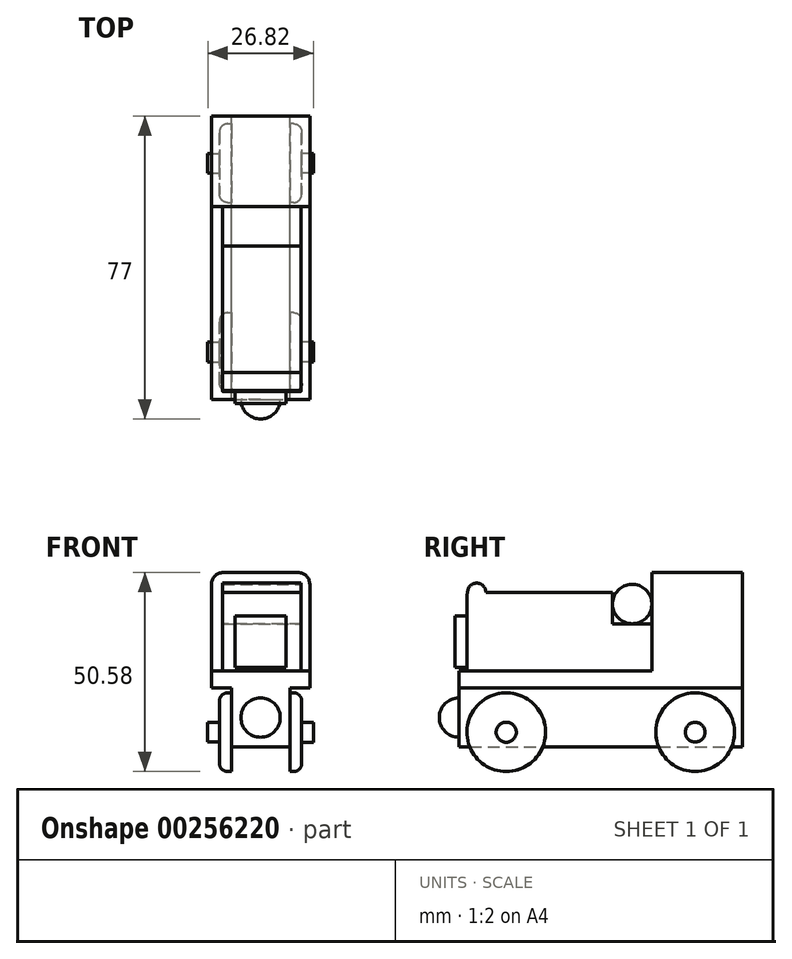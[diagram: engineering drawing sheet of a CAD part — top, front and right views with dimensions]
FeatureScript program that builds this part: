
annotation { "Feature Type Name" : "Feature", "Feature Type Description" : "" }
export const myFeature = defineFeature(function(context is Context, id is Id, definition is map)
    precondition{}
    {
        {
            var Q0;
            Q0=qCreatedBy(makeId("Front.planeOp"),FACE);
            var sketch = newSketch(context, id + "F0", { "sketchPlane" : qUnion([Q0])});
            skLineSegment(sketch, "E0.bottom", {"start": v(-9.68, 12.6) * mm, "end": v(10.32, 12.6) * mm});
            skLineSegment(sketch, "E0.top", {"start": v(-9.68, -7.4) * mm, "end": v(10.32, -7.4) * mm});
            skLineSegment(sketch, "E0.left", {"start": v(-9.68, 12.6) * mm, "end": v(-9.68, -7.4) * mm});
            skLineSegment(sketch, "E0.right", {"start": v(10.32, 12.6) * mm, "end": v(10.32, -7.4) * mm});
            skSolve(sketch);
        }
        {
            var Q0;
            Q0 = qSketchRegion(id + "F0", true);
            extrude(context, id + "F1", {"entities" : qUnion([Q0]), "endBound" : BoundingType.SYMMETRIC, "depth" : 10 * mm});
        }
        {
            var Q0;
            Q0=makeQuery(id+"F1.opExtrude","CAP_FACE",FACE,{"disambiguationData":[OSD([sQuery(id+"F0.wireOp",EDGE,"E0.bottom"),sQuery(id+"F0.wireOp",EDGE,"E0.top"),sQuery(id+"F0.wireOp",EDGE,"E0.left"),sQuery(id+"F0.wireOp",EDGE,"E0.right")])],"isStart":true});
            var sketch = newSketch(context, id + "F2", { "sketchPlane" : qUnion([Q0])});
            skLineSegment(sketch, "E1.bottom", {"start": v(-10.32, 12.6) * mm, "end": v(9.68, 12.6) * mm});
            skLineSegment(sketch, "E1.top", {"start": v(-10.32, 4.6) * mm, "end": v(9.68, 4.6) * mm});
            skLineSegment(sketch, "E1.left", {"start": v(-10.32, 12.6) * mm, "end": v(-10.32, 4.6) * mm});
            skLineSegment(sketch, "E1.right", {"start": v(9.68, 12.6) * mm, "end": v(9.68, 4.6) * mm});
            skSolve(sketch);
        }
        {
            var Q0;
            Q0 = qSketchRegion(id + "F2", true);
            extrude(context, id + "F3", {"entities" : qUnion([Q0]), "operationType" : NewBodyOperationType.ADD, "depth" : 27 * mm});
        }
        {
            var Q0;
            Q0=makeQuery(id+"F1.opExtrude","CAP_FACE",FACE,{"disambiguationData":[OSD([sQuery(id+"F0.wireOp",EDGE,"E0.bottom"),sQuery(id+"F0.wireOp",EDGE,"E0.top"),sQuery(id+"F0.wireOp",EDGE,"E0.left"),sQuery(id+"F0.wireOp",EDGE,"E0.right")])],"isStart":true});
            var sketch = newSketch(context, id + "F4", { "sketchPlane" : qUnion([Q0])});
            skLineSegment(sketch, "E2.bottom", {"start": v(-10.32, 4.6) * mm, "end": v(9.68, 4.6) * mm});
            skLineSegment(sketch, "E2.top", {"start": v(-10.32, -7.4) * mm, "end": v(9.68, -7.4) * mm});
            skLineSegment(sketch, "E2.left", {"start": v(-10.32, 4.6) * mm, "end": v(-10.32, -7.4) * mm});
            skLineSegment(sketch, "E2.right", {"start": v(9.68, 4.6) * mm, "end": v(9.68, -7.4) * mm});
            skSolve(sketch);
        }
        {
            var Q0;
            Q0 = qSketchRegion(id + "F4", true);
            extrude(context, id + "F5", {"entities" : qUnion([Q0]), "operationType" : NewBodyOperationType.ADD, "depth" : 37 * mm});
        }
        {
            var Q0;
            Q0=qCreatedBy(makeId("Front.planeOp"),FACE);
            var sketch = newSketch(context, id + "F6", { "sketchPlane" : qUnion([Q0])});
            skLineSegment(sketch, "E3.bottom", {"start": v(-12.5, -7.4) * mm, "end": v(12.5, -7.4) * mm});
            skLineSegment(sketch, "E3.top", {"start": v(-12.5, -11.76) * mm, "end": v(12.5, -11.76) * mm});
            skLineSegment(sketch, "E3.left", {"start": v(-12.5, -7.4) * mm, "end": v(-12.5, -11.76) * mm});
            skLineSegment(sketch, "E3.right", {"start": v(12.5, -7.4) * mm, "end": v(12.5, -11.76) * mm});
            skPoint(sketch, "E3.middle", {"position": v(0, -9.58) * mm});
            skSolve(sketch);
        }
        {
            var Q0;
            Q0=makeQuery(id+"F6.imprint","IMPRINT",FACE,{"disambiguationData":[TD([[makeQuery(id+"F6.imprint","IMPRINT",EDGE,{"derivedFrom":sQuery(id+"F6.wireOp",EDGE,"E3.bottom")}),-1.0]])]});
            extrude(context, id + "F7", {"entities" : qUnion([Q0]), "operationType" : NewBodyOperationType.ADD, "oppositeDirection" : true, "depth" : 65 * mm});
        }
        {
            var Q0;
            Q0=makeQuery(id+"F7.opExtrude","CAP_FACE",FACE,{"disambiguationData":[OSD([sQuery(id+"F6.wireOp",EDGE,"E3.bottom"),sQuery(id+"F6.wireOp",EDGE,"E3.top"),sQuery(id+"F6.wireOp",EDGE,"E3.left"),sQuery(id+"F6.wireOp",EDGE,"E3.right")])],"isStart":true});
            var sketch = newSketch(context, id + "F8", { "sketchPlane" : qUnion([Q0])});
            skLineSegment(sketch, "E4.bottom", {"start": v(-12.5, -7.4) * mm, "end": v(12.5, -7.4) * mm});
            skLineSegment(sketch, "E4.top", {"start": v(-12.5, -11.76) * mm, "end": v(12.5, -11.76) * mm});
            skLineSegment(sketch, "E4.left", {"start": v(-12.5, -7.4) * mm, "end": v(-12.5, -11.76) * mm});
            skLineSegment(sketch, "E4.right", {"start": v(12.5, -7.4) * mm, "end": v(12.5, -11.76) * mm});
            skSolve(sketch);
        }
        {
            var Q0;
            Q0 = qSketchRegion(id + "F8", true);
            extrude(context, id + "F9", {"entities" : qUnion([Q0]), "operationType" : NewBodyOperationType.ADD, "depth" : 7 * mm});
        }
        {
            var Q0;
            Q0=makeQuery(id+"F9.boolean.opBoolean","MERGE",FACE,{"derivedFrom":[makeQuery(id+"F7.opExtrude","SWEPT_FACE",FACE,{"disambiguationData":[OSD([sQuery(id+"F6.wireOp",EDGE,"E3.bottom")])]}),makeQuery(id+"F9.opExtrude","SWEPT_FACE",FACE,{"disambiguationData":[OSD([sQuery(id+"F8.wireOp",EDGE,"E4.bottom")])]})]});
            var sketch = newSketch(context, id + "F10", { "sketchPlane" : qUnion([Q0])});
            skLineSegment(sketch, "E5.bottom", {"start": v(-12.5, 42) * mm, "end": v(12.5, 42) * mm});
            skLineSegment(sketch, "E5.top", {"start": v(-12.5, 65) * mm, "end": v(12.5, 65) * mm});
            skLineSegment(sketch, "E5.left", {"start": v(-12.5, 42) * mm, "end": v(-12.5, 65) * mm});
            skLineSegment(sketch, "E5.right", {"start": v(12.5, 42) * mm, "end": v(12.5, 65) * mm});
            skSolve(sketch);
        }
        {
            var Q0;
            Q0 = qSketchRegion(id + "F10", true);
            extrude(context, id + "F11", {"entities" : qUnion([Q0]), "operationType" : NewBodyOperationType.ADD, "depth" : 25 * mm});
        }
        {
            var Q0;
            Q0=makeQuery(id+"F5.boolean.opBoolean","MERGE",FACE,{"derivedFrom":[makeQuery(id+"F3.boolean.opBoolean","MERGE",FACE,{"derivedFrom":[makeQuery(id+"F1.opExtrude","SWEPT_FACE",FACE,{"disambiguationData":[OSD([sQuery(id+"F0.wireOp",EDGE,"E0.right")])]}),makeQuery(id+"F3.opExtrude","SWEPT_FACE",FACE,{"disambiguationData":[OSD([sQuery(id+"F2.wireOp",EDGE,"E1.left")])]})]}),makeQuery(id+"F5.opExtrude","SWEPT_FACE",FACE,{"disambiguationData":[OSD([sQuery(id+"F4.wireOp",EDGE,"E2.left")])]})]});
            var sketch = newSketch(context, id + "F12", { "sketchPlane" : qUnion([Q0])});
            skLineSegment(sketch, "E6", {"start": v(42, 4.6) * mm, "end": v(42, 17.55) * mm, "construction": true});
            skPoint(sketch, "E7.first.point", {"position": v(37, 4.6) * mm});
            skPoint(sketch, "E7.second.point", {"position": v(32, 8.6) * mm});
            skPoint(sketch, "E7.third.point", {"position": v(42, 9.37) * mm});
            skCircle(sketch, "E8", {"center": v(37, 9.6) * mm, "radius": 5 * mm});
            skPoint(sketch, "E8.third.point", {"position": v(32, 9.37) * mm});
            skSolve(sketch);
        }
        {
            var Q0;
            Q0 = qSketchRegion(id + "F12", true);
            extrude(context, id + "F13", {"entities" : qUnion([Q0]), "oppositeDirection" : true, "depth" : 20 * mm});
        }
        {
            var Q0;
            Q0=makeQuery(id+"F9.boolean.opBoolean","MERGE",FACE,{"derivedFrom":[makeQuery(id+"F7.opExtrude","SWEPT_FACE",FACE,{"disambiguationData":[OSD([sQuery(id+"F6.wireOp",EDGE,"E3.top")])]}),makeQuery(id+"F9.opExtrude","SWEPT_FACE",FACE,{"disambiguationData":[OSD([sQuery(id+"F8.wireOp",EDGE,"E4.top")])]})]});
            var sketch = newSketch(context, id + "F14", { "sketchPlane" : qUnion([Q0])});
            skLineSegment(sketch, "E9", {"start": v(-12.5, -29) * mm, "end": v(-7.5, -29) * mm, "construction": true});
            skLineSegment(sketch, "E10", {"start": v(12.5, -29) * mm, "end": v(7.5, -29) * mm, "construction": true});
            skPoint(sketch, "E10.endSnap0", {"position": v(12.5, -29) * mm});
            skLineSegment(sketch, "E11.bottom", {"start": v(7.41, 7) * mm, "end": v(-7.41, 7) * mm});
            skLineSegment(sketch, "E11.top", {"start": v(7.41, -65) * mm, "end": v(-7.41, -65) * mm});
            skLineSegment(sketch, "E11.left", {"start": v(7.41, 7) * mm, "end": v(7.41, -65) * mm});
            skLineSegment(sketch, "E11.right", {"start": v(-7.41, 7) * mm, "end": v(-7.41, -65) * mm});
            skPoint(sketch, "E11.middle", {"position": v(0, -29) * mm});
            skSolve(sketch);
        }
        {
            var Q0;
            Q0 = qSketchRegion(id + "F14", true);
            extrude(context, id + "F15", {"entities" : qUnion([Q0]), "operationType" : NewBodyOperationType.ADD, "depth" : 15 * mm});
        }
        {
            var Q0;
            Q0=makeQuery(id+"FdtICwUZpQ81nrQ_1.boolean.opBoolean","MERGE",FACE,{"derivedFrom":[makeQuery(id+"F5.boolean.opBoolean","MERGE",FACE,{"derivedFrom":[makeQuery(id+"F3.boolean.opBoolean","MERGE",FACE,{"derivedFrom":[makeQuery(id+"F1.opExtrude","SWEPT_FACE",FACE,{"disambiguationData":[OSD([sQuery(id+"F0.wireOp",EDGE,"E0.right")])]}),makeQuery(id+"F3.opExtrude","SWEPT_FACE",FACE,{"disambiguationData":[OSD([sQuery(id+"F2.wireOp",EDGE,"E1.left")])]})]}),makeQuery(id+"F5.opExtrude","SWEPT_FACE",FACE,{"disambiguationData":[OSD([sQuery(id+"F4.wireOp",EDGE,"E2.left")])]})]}),makeQuery(id+"FdtICwUZpQ81nrQ_1.opExtrude","CAP_FACE",FACE,{"disambiguationData":[OSD([sQuery(id+"F12.wireOp",EDGE,"ziEQ1xZp-qsWu-kRBI-7kLP-nA51zgmRD1Y3")])],"isStart":true})]});
            var sketch = newSketch(context, id + "F16", { "sketchPlane" : qUnion([Q0])});
            skLineSegment(sketch, "E12", {"start": v(-5, 12.6) * mm, "end": v(0, 12.6) * mm});
            skArc(sketch, "E13", {"start": v(-0.2, 12.6) * mm, "mid": v(-2.5, 14.9) * mm, "end": v(-4.8, 12.6) * mm});
            skLineSegment(sketch, "E14", {"start": v(-5, 12.6) * mm, "end": v(0, 12.6) * mm, "construction": true});
            skSolve(sketch);
        }
        {
            var Q0;
            {var subQ0=sQuery(id+"F16.wireOp",EDGE,"E13");Q0=makeQuery(id+"F16.imprint","IMPRINT",FACE,{"disambiguationData":[TD([[makeQuery(id+"F16.imprint","IMPRINT",EDGE,{"derivedFrom":subQ0}),1.0]])]});}
            var Q1;
            Q1=sQuery(id+"F16.wireOp",EDGE,"E13");
            extrude(context, id + "F17", {"entities" : qUnion([Q0]), "operationType" : NewBodyOperationType.ADD, "surfaceEntities" : qUnion([Q1]), "oppositeDirection" : true, "depth" : 20 * mm});
        }
        {
            var Q0;
            Q0=makeQuery(id+"F1.opExtrude","CAP_EDGE",EDGE,{"disambiguationData":[OSD([sQuery(id+"F0.wireOp",EDGE,"E0.bottom")])],"isStart":false});
            fillet(context, id + "F18", {"entities" : qUnion([Q0]), "radius" : 5 * mm, "tangentPropagation" : true, "allowEdgeOverflow" : false});
        }
        {
            var Q0;
            Q0=makeQuery(id+"F15.opExtrude","SWEPT_FACE",FACE,{"disambiguationData":[OSD([sQuery(id+"F14.wireOp",EDGE,"E11.left")])]});
            var sketch = newSketch(context, id + "F19", { "sketchPlane" : qUnion([Q0])});
            skLineSegment(sketch, "E15", {"start": v(-7, -11.76) * mm, "end": v(5, -11.76) * mm, "construction": true});
            skLineSegment(sketch, "E16", {"start": v(5, -11.76) * mm, "end": v(5, -26.76) * mm, "construction": true});
            skLineSegment(sketch, "E17", {"start": v(65, -11.76) * mm, "end": v(53, -11.76) * mm, "construction": true});
            skLineSegment(sketch, "E18", {"start": v(53, -11.76) * mm, "end": v(53, -26.76) * mm, "construction": true});
            skLineSegment(sketch, "E19", {"start": v(-7, -22.98) * mm, "end": v(65, -22.98) * mm, "construction": true});
            skCircle(sketch, "E20", {"center": v(5, -22.98) * mm, "radius": 10 * mm});
            skCircle(sketch, "E21", {"center": v(53, -22.98) * mm, "radius": 10 * mm});
            skSolve(sketch);
        }
        {
            var Q0;
            Q0 = qSketchRegion(id + "F19", true);
            extrude(context, id + "F20", {"entities" : qUnion([Q0]), "operationType" : NewBodyOperationType.ADD, "depth" : 3 * mm});
        }
        {
            var Q0;
            Q0=makeQuery(id+"F15.opExtrude","SWEPT_FACE",FACE,{"disambiguationData":[OSD([sQuery(id+"F14.wireOp",EDGE,"E11.right")])]});
            var sketch = newSketch(context, id + "F21", { "sketchPlane" : qUnion([Q0])});
            skLineSegment(sketch, "E22", {"start": v(-65, -26.76) * mm, "end": v(7, -26.76) * mm, "construction": true});
            skArc(sketch, "E23.0", {"start": v(-62.26, -26.76) * mm, "mid": v(-53, -12.98) * mm, "end": v(-43.74, -26.76) * mm});
            skArc(sketch, "E24.0", {"start": v(-14.26, -26.76) * mm, "mid": v(-5, -12.98) * mm, "end": v(4.26, -26.76) * mm});
            skCircle(sketch, "E25", {"center": v(-53, -22.98) * mm, "radius": 10 * mm});
            skCircle(sketch, "E26", {"center": v(-5, -22.98) * mm, "radius": 10 * mm});
            skSolve(sketch);
        }
        {
            var Q0;
            Q0 = qSketchRegion(id + "F21", true);
            extrude(context, id + "F22", {"entities" : qUnion([Q0]), "operationType" : NewBodyOperationType.ADD, "depth" : 3 * mm});
        }
        {
            var Q0;
            Q0=makeQuery(id+"F15.boolean.opBoolean","MERGE",FACE,{"derivedFrom":[makeQuery(id+"F9.opExtrude","CAP_FACE",FACE,{"disambiguationData":[OSD([sQuery(id+"F8.wireOp",EDGE,"E4.bottom"),sQuery(id+"F8.wireOp",EDGE,"E4.top"),sQuery(id+"F8.wireOp",EDGE,"E4.left"),sQuery(id+"F8.wireOp",EDGE,"E4.right")])],"isStart":false}),makeQuery(id+"F15.opExtrude","SWEPT_FACE",FACE,{"disambiguationData":[OSD([sQuery(id+"F14.wireOp",EDGE,"E11.bottom")])]})]});
            var sketch = newSketch(context, id + "F23", { "sketchPlane" : qUnion([Q0])});
            skArc(sketch, "E27", {"start": v(0, -14.26) * mm, "mid": v(-5, -19.26) * mm, "end": v(0, -24.26) * mm});
            skPoint(sketch, "E27.centerSnap0", {"position": v(7.41, -19.26) * mm});
            skLineSegment(sketch, "E28", {"start": v(0, -14.26) * mm, "end": v(0, -24.26) * mm, "construction": true});
            skLineSegment(sketch, "E29", {"start": v(0, -14.26) * mm, "end": v(0, -24.26) * mm});
            skSolve(sketch);
        }
        {
            var Q0;
            Q0 = qSketchRegion(id + "F23", true);
            var Q1;
            Q1=sQuery(id+"F23.wireOp",EDGE,"E27");
            var Q2;
            Q2=sQuery(id+"F23.wireOp",EDGE,"E29");
            revolve(context, id + "F24", {"operationType" : NewBodyOperationType.ADD, "entities" : qUnion([Q0]), "surfaceEntities" : qUnion([Q1]), "axis" : qUnion([Q2]), "revolveType" : RevolveType.FULL});
        }
        {
            var Q0;
            Q0=makeQuery(id+"F20.opExtrude","CAP_FACE",FACE,{"disambiguationData":[OSD([sQuery(id+"F19.wireOp",EDGE,"E20")])],"isStart":false});
            var sketch = newSketch(context, id + "F25", { "sketchPlane" : qUnion([Q0])});
            skCircle(sketch, "E30", {"center": v(5, -22.98) * mm, "radius": 2.55 * mm});
            skSolve(sketch);
        }
        {
            var Q0;
            Q0 = qSketchRegion(id + "F25", true);
            extrude(context, id + "F26", {"entities" : qUnion([Q0]), "operationType" : NewBodyOperationType.ADD, "depth" : 3 * mm});
        }
        {
            var Q0;
            Q0=makeQuery(id+"F20.opExtrude","CAP_FACE",FACE,{"disambiguationData":[OSD([sQuery(id+"F19.wireOp",EDGE,"E21")])],"isStart":false});
            var sketch = newSketch(context, id + "F27", { "sketchPlane" : qUnion([Q0])});
            skCircle(sketch, "E31", {"center": v(53, -22.98) * mm, "radius": 2.5 * mm});
            skSolve(sketch);
        }
        {
            var Q0;
            Q0 = qSketchRegion(id + "F27", true);
            extrude(context, id + "F28", {"entities" : qUnion([Q0]), "operationType" : NewBodyOperationType.ADD, "depth" : 3 * mm});
        }
        {
            var Q0;
            Q0=makeQuery(id+"F22.opExtrude","CAP_FACE",FACE,{"disambiguationData":[OSD([sQuery(id+"F21.wireOp",EDGE,"E26")])],"isStart":false});
            var sketch = newSketch(context, id + "F29", { "sketchPlane" : qUnion([Q0])});
            skCircle(sketch, "E32", {"center": v(-5, -22.98) * mm, "radius": 2.5 * mm});
            skSolve(sketch);
        }
        {
            var Q0;
            Q0 = qSketchRegion(id + "F29", true);
            extrude(context, id + "F30", {"entities" : qUnion([Q0]), "operationType" : NewBodyOperationType.ADD, "depth" : 3 * mm});
        }
        {
            var Q0;
            Q0=makeQuery(id+"F22.opExtrude","CAP_FACE",FACE,{"disambiguationData":[OSD([sQuery(id+"F21.wireOp",EDGE,"E25")])],"isStart":false});
            var sketch = newSketch(context, id + "F31", { "sketchPlane" : qUnion([Q0])});
            skCircle(sketch, "E33", {"center": v(-53, -22.98) * mm, "radius": 2.5 * mm});
            skSolve(sketch);
        }
        {
            var Q0;
            Q0 = qSketchRegion(id + "F31", true);
            extrude(context, id + "F32", {"entities" : qUnion([Q0]), "operationType" : NewBodyOperationType.ADD, "depth" : 3 * mm});
        }
        {
            var Q0;
            Q0=makeQuery(id+"F22.opExtrude","CAP_EDGE",EDGE,{"disambiguationData":[OSD([sQuery(id+"F21.wireOp",EDGE,"E25")])],"isStart":false});
            var Q1;
            Q1=makeQuery(id+"F22.opExtrude","CAP_EDGE",EDGE,{"disambiguationData":[OSD([sQuery(id+"F21.wireOp",EDGE,"E26")])],"isStart":false});
            var Q2;
            Q2=makeQuery(id+"F20.opExtrude","CAP_EDGE",EDGE,{"disambiguationData":[OSD([sQuery(id+"F19.wireOp",EDGE,"E21")])],"isStart":false});
            var Q3;
            Q3=makeQuery(id+"F20.opExtrude","CAP_EDGE",EDGE,{"disambiguationData":[OSD([sQuery(id+"F19.wireOp",EDGE,"E20")])],"isStart":false});
            fillet(context, id + "F33", {"entities" : qUnion([Q0, Q1, Q2, Q3]), "radius" : 2 * mm, "tangentPropagation" : true, "allowEdgeOverflow" : false});
        }
        {
            var Q0;
            Q0=makeQuery(id+"F11.opExtrude","CAP_EDGE",EDGE,{"disambiguationData":[OSD([sQuery(id+"F10.wireOp",EDGE,"E5.right")])],"isStart":false});
            var Q1;
            Q1=makeQuery(id+"F11.opExtrude","CAP_EDGE",EDGE,{"disambiguationData":[OSD([sQuery(id+"F10.wireOp",EDGE,"E5.left")])],"isStart":false});
            fillet(context, id + "F34", {"entities" : qUnion([Q0, Q1]), "radius" : 3 * mm, "tangentPropagation" : true, "allowEdgeOverflow" : false});
        }
        {
            var Q0;
            Q0=makeQuery(id+"F1.opExtrude","CAP_FACE",FACE,{"disambiguationData":[OSD([sQuery(id+"F0.wireOp",EDGE,"E0.bottom"),sQuery(id+"F0.wireOp",EDGE,"E0.top"),sQuery(id+"F0.wireOp",EDGE,"E0.left"),sQuery(id+"F0.wireOp",EDGE,"E0.right")])],"isStart":false});
            var sketch = newSketch(context, id + "F35", { "sketchPlane" : qUnion([Q0])});
            skLineSegment(sketch, "E34.bottom", {"start": v(-6.5, 6.5) * mm, "end": v(6.5, 6.5) * mm});
            skLineSegment(sketch, "E34.top", {"start": v(-6.5, -6.5) * mm, "end": v(6.5, -6.5) * mm});
            skLineSegment(sketch, "E34.left", {"start": v(-6.5, 6.5) * mm, "end": v(-6.5, -6.5) * mm});
            skLineSegment(sketch, "E34.right", {"start": v(6.5, 6.5) * mm, "end": v(6.5, -6.5) * mm});
            skPoint(sketch, "E34.middle", {"position": v(0, 0) * mm});
            skSolve(sketch);
        }
        {
            var Q0;
            Q0 = qSketchRegion(id + "F35", true);
            extrude(context, id + "F36", {"entities" : qUnion([Q0]), "operationType" : NewBodyOperationType.ADD, "depth" : 3 * mm});
        }
    });
